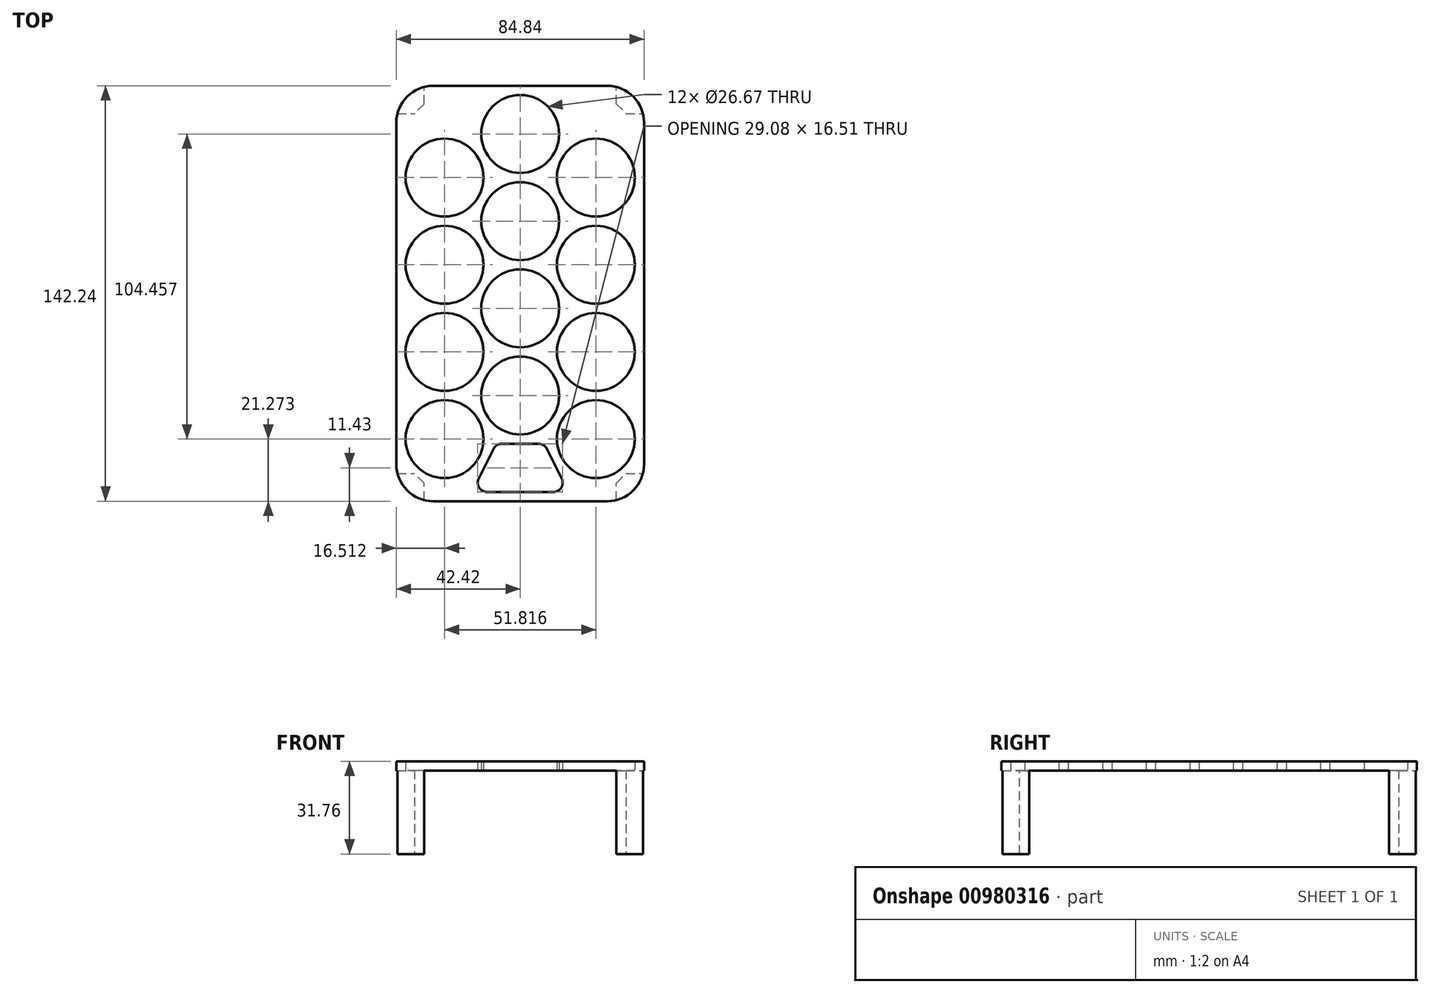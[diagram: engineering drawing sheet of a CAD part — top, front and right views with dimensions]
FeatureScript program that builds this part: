
annotation { "Feature Type Name" : "Feature", "Feature Type Description" : "" }
export const myFeature = defineFeature(function(context is Context, id is Id, definition is map)
    precondition{}
    {
        {
            var Q0;
            Q0=qCreatedBy(makeId("Front.planeOp"),FACE);
            var sketch = newSketch(context, id + "F0", { "sketchPlane" : qUnion([Q0])});
            skLineSegment(sketch, "E0.bottom", {"start": v(-42.42, -15.88) * mm, "end": v(-32.9, -15.88) * mm});
            skLineSegment(sketch, "E0.top", {"start": v(-42.42, 15.87) * mm, "end": v(42.42, 15.88) * mm});
            skLineSegment(sketch, "E0.left", {"start": v(-42.42, -15.88) * mm, "end": v(-42.42, 15.87) * mm});
            skLineSegment(sketch, "E0.right", {"start": v(42.42, -15.87) * mm, "end": v(42.42, 15.88) * mm});
            skPoint(sketch, "E0.middle", {"position": v(0, 0) * mm});
            skLineSegment(sketch, "E1.top", {"start": v(-32.9, 12.7) * mm, "end": v(32.9, 12.7) * mm});
            skLineSegment(sketch, "E1.left", {"start": v(-32.9, -15.88) * mm, "end": v(-32.9, 12.7) * mm});
            skLineSegment(sketch, "E1.right", {"start": v(32.9, -15.87) * mm, "end": v(32.9, 12.7) * mm});
            skLineSegment(sketch, "E2.trimOffspring", {"start": v(32.9, -15.87) * mm, "end": v(42.42, -15.87) * mm});
            skPoint(sketch, "E3.visualSharp", {"position": v(-32.9, 12.7) * mm});
            skLineSegment(sketch, "E3.filletArc", {"start": v(-32.9, 12.7) * mm, "end": v(-32.9, 12.7) * mm});
            skPoint(sketch, "E4.visualSharp", {"position": v(32.9, 12.7) * mm});
            skLineSegment(sketch, "E5", {"start": v(32.9, 12.7) * mm, "end": v(32.9, 12.7) * mm});
            skSolve(sketch);
        }
        {
            var Q0;
            Q0 = qSketchRegion(id + "F0", true);
            extrude(context, id + "F1", {"entities" : qUnion([Q0]), "depth" : 142.24 * mm, "offsetDistance" : 25.4 * mm});
        }
        {
            var Q0;
            Q0=makeQuery(id+"F1.opExtrude","SWEPT_FACE",FACE,{"disambiguationData":[OSD([sQuery(id+"F0.wireOp",EDGE,"E0.right")])]});
            var sketch = newSketch(context, id + "F2", { "sketchPlane" : qUnion([Q0])});
            skLineSegment(sketch, "E6.bottom", {"start": v(-132.72, -15.87) * mm, "end": v(-9.52, -15.87) * mm});
            skLineSegment(sketch, "E6.top", {"start": v(-132.72, 12.7) * mm, "end": v(-9.53, 12.7) * mm});
            skLineSegment(sketch, "E6.left", {"start": v(-132.72, -15.87) * mm, "end": v(-132.72, 12.7) * mm});
            skLineSegment(sketch, "E6.right", {"start": v(-9.52, -15.87) * mm, "end": v(-9.53, 12.7) * mm});
            skPoint(sketch, "E7.visualSharp", {"position": v(-132.72, 12.7) * mm});
            skLineSegment(sketch, "E7.filletArc", {"start": v(-132.72, 12.7) * mm, "end": v(-132.72, 12.7) * mm});
            skPoint(sketch, "E8.visualSharp", {"position": v(-9.53, 12.7) * mm});
            skLineSegment(sketch, "E8.filletArc", {"start": v(-9.53, 12.7) * mm, "end": v(-9.53, 12.7) * mm});
            skSolve(sketch);
        }
        {
            var Q0;
            Q0 = qSketchRegion(id + "F2", true);
            extrude(context, id + "F3", {"entities" : qUnion([Q0]), "operationType" : NewBodyOperationType.REMOVE, "endBound" : BoundingType.THROUGH_ALL, "oppositeDirection" : true, "depth" : 25.4 * mm, "offsetDistance" : 25.4 * mm});
        }
        {
            var Q0;
            Q0=makeQuery(id+"F1.opExtrude","SWEPT_FACE",FACE,{"disambiguationData":[OSD([sQuery(id+"F0.wireOp",EDGE,"E0.top")])]});
            var sketch = newSketch(context, id + "F4", { "sketchPlane" : qUnion([Q0])});
            skCircle(sketch, "E9", {"center": v(0, -16.51) * mm, "radius": 13.34 * mm});
            skCircle(sketch, "E10", {"center": v(0, -46.36) * mm, "radius": 13.34 * mm});
            skCircle(sketch, "E11", {"center": v(0, -76.2) * mm, "radius": 13.34 * mm});
            skCircle(sketch, "E12", {"center": v(0, -106.05) * mm, "radius": 13.34 * mm});
            skCircle(sketch, "E13", {"center": v(-25.9, -120.97) * mm, "radius": 13.34 * mm});
            skCircle(sketch, "E14", {"center": v(-25.9, -91.12) * mm, "radius": 13.34 * mm});
            skCircle(sketch, "E15", {"center": v(-25.9, -61.28) * mm, "radius": 13.34 * mm});
            skCircle(sketch, "E16", {"center": v(-25.9, -31.43) * mm, "radius": 13.34 * mm});
            skCircle(sketch, "E17.MirrorC", {"center": v(25.9, -120.97) * mm, "radius": 13.34 * mm});
            skCircle(sketch, "E18.MirrorC", {"center": v(25.9, -91.12) * mm, "radius": 13.34 * mm});
            skCircle(sketch, "E19.MirrorC", {"center": v(25.9, -61.28) * mm, "radius": 13.34 * mm});
            skCircle(sketch, "E20.MirrorC", {"center": v(25.9, -31.43) * mm, "radius": 13.34 * mm});
            skLineSegment(sketch, "E21", {"start": v(-11.37, -139.06) * mm, "end": v(11.37, -139.06) * mm});
            skLineSegment(sketch, "E22", {"start": v(-6.28, -122.56) * mm, "end": v(6.28, -122.56) * mm});
            skLineSegment(sketch, "E23", {"start": v(-14.2, -134.47) * mm, "end": v(-9.11, -124.3) * mm});
            skLineSegment(sketch, "E24", {"start": v(9.11, -124.3) * mm, "end": v(14.2, -134.47) * mm});
            skPoint(sketch, "E25.visualSharp", {"position": v(-16.51, -139.06) * mm});
            skArc(sketch, "E25.filletArc", {"start": v(-14.2, -134.47) * mm, "mid": v(-14.07, -137.56) * mm, "end": v(-11.37, -139.06) * mm});
            skPoint(sketch, "E26.visualSharp", {"position": v(16.51, -139.06) * mm});
            skArc(sketch, "E26.filletArc", {"start": v(11.37, -139.06) * mm, "mid": v(14.07, -137.56) * mm, "end": v(14.2, -134.47) * mm});
            skPoint(sketch, "E27.visualSharp", {"position": v(-8.24, -122.56) * mm});
            skArc(sketch, "E27.filletArc", {"start": v(-6.28, -122.56) * mm, "mid": v(-7.94, -123.03) * mm, "end": v(-9.11, -124.3) * mm});
            skPoint(sketch, "E28.visualSharp", {"position": v(8.24, -122.56) * mm});
            skArc(sketch, "E28.filletArc", {"start": v(9.11, -124.3) * mm, "mid": v(7.94, -123.03) * mm, "end": v(6.28, -122.56) * mm});
            skSolve(sketch);
        }
        {
            var Q0;
            Q0 = qSketchRegion(id + "F4", true);
            extrude(context, id + "F5", {"entities" : qUnion([Q0]), "operationType" : NewBodyOperationType.REMOVE, "endBound" : BoundingType.SYMMETRIC, "depth" : 12.7 * mm, "offsetDistance" : 25.4 * mm});
        }
        {
            var Q0;
            Q0=makeQuery(id+"F1.opExtrude","CAP_EDGE",EDGE,{"disambiguationData":[OSD([sQuery(id+"F0.wireOp",EDGE,"E0.left")])],"isStart":false});
            var Q1;
            Q1=makeQuery(id+"F1.opExtrude","CAP_EDGE",EDGE,{"disambiguationData":[OSD([sQuery(id+"F0.wireOp",EDGE,"E0.right")])],"isStart":false});
            var Q2;
            Q2=makeQuery(id+"F1.opExtrude","CAP_EDGE",EDGE,{"disambiguationData":[OSD([sQuery(id+"F0.wireOp",EDGE,"E0.right")])],"isStart":true});
            var Q3;
            Q3=makeQuery(id+"F1.opExtrude","CAP_EDGE",EDGE,{"disambiguationData":[OSD([sQuery(id+"F0.wireOp",EDGE,"E0.left")])],"isStart":true});
            fillet(context, id + "F6", {"entities" : qUnion([Q0, Q1, Q2, Q3]), "radius" : 12.7 * mm, "tangentPropagation" : true, "allowEdgeOverflow" : false});
        }
        {
            var Q0;
            Q0=makeQuery(id+"F3.boolean.opBoolean","INTERSECT",EDGE,{"derivedFrom":[makeQuery(id+"F1.opExtrude","SWEPT_FACE",FACE,{"disambiguationData":[OSD([sQuery(id+"F0.wireOp",EDGE,"E1.right")])]}),makeQuery(id+"F3.opExtrude","SWEPT_FACE",FACE,{"disambiguationData":[OSD([sQuery(id+"F2.wireOp",EDGE,"E6.left")])]})]});
            var Q1;
            Q1=makeQuery(id+"F3.boolean.opBoolean","INTERSECT",EDGE,{"derivedFrom":[makeQuery(id+"F1.opExtrude","SWEPT_FACE",FACE,{"disambiguationData":[OSD([sQuery(id+"F0.wireOp",EDGE,"E1.left")])]}),makeQuery(id+"F3.opExtrude","SWEPT_FACE",FACE,{"disambiguationData":[OSD([sQuery(id+"F2.wireOp",EDGE,"E6.left")])]})]});
            var Q2;
            Q2=makeQuery(id+"F3.boolean.opBoolean","INTERSECT",EDGE,{"derivedFrom":[makeQuery(id+"F1.opExtrude","SWEPT_FACE",FACE,{"disambiguationData":[OSD([sQuery(id+"F0.wireOp",EDGE,"E1.right")])]}),makeQuery(id+"F3.opExtrude","SWEPT_FACE",FACE,{"disambiguationData":[OSD([sQuery(id+"F2.wireOp",EDGE,"E6.right")])]})]});
            var Q3;
            Q3=makeQuery(id+"F3.boolean.opBoolean","INTERSECT",EDGE,{"derivedFrom":[makeQuery(id+"F1.opExtrude","SWEPT_FACE",FACE,{"disambiguationData":[OSD([sQuery(id+"F0.wireOp",EDGE,"E1.left")])]}),makeQuery(id+"F3.opExtrude","SWEPT_FACE",FACE,{"disambiguationData":[OSD([sQuery(id+"F2.wireOp",EDGE,"E6.right")])]})]});
            chamfer(context, id + "F7", {"entities" : qUnion([Q0, Q1, Q2, Q3]), "width" : 3.3 * mm, "tangentPropagation" : true});
        }
    });
